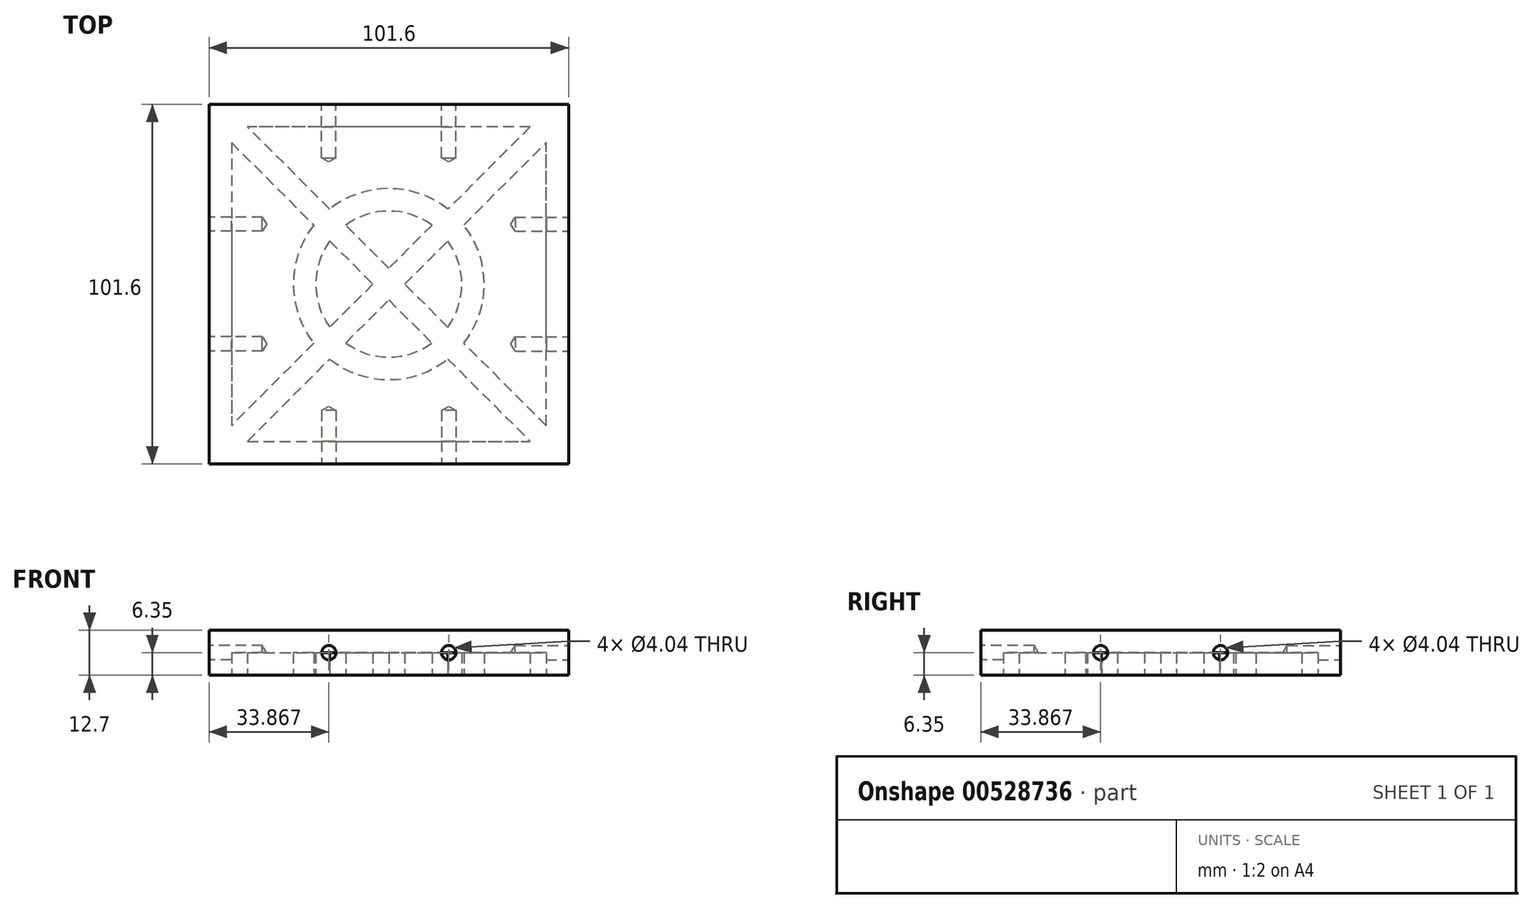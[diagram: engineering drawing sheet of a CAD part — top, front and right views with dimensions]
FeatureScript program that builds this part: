
annotation { "Feature Type Name" : "Feature", "Feature Type Description" : "" }
export const myFeature = defineFeature(function(context is Context, id is Id, definition is map)
    precondition{}
    {
        {
            var Q0;
            Q0=qCreatedBy(makeId("Top.planeOp"),FACE);
            var sketch = newSketch(context, id + "F0", { "sketchPlane" : qUnion([Q0])});
            skLineSegment(sketch, "E0.bottom", {"start": v(50.8, -50.8) * mm, "end": v(-50.8, -50.8) * mm});
            skLineSegment(sketch, "E0.top", {"start": v(50.8, 50.8) * mm, "end": v(-50.8, 50.8) * mm});
            skLineSegment(sketch, "E0.left", {"start": v(50.8, -50.8) * mm, "end": v(50.8, 50.8) * mm});
            skLineSegment(sketch, "E0.right", {"start": v(-50.8, -50.8) * mm, "end": v(-50.8, 50.8) * mm});
            skPoint(sketch, "E0.middle", {"position": v(0, 0) * mm});
            skSolve(sketch);
        }
        {
            var Q0;
            Q0 = qSketchRegion(id + "F0", true);
            extrude(context, id + "F1", {"entities" : qUnion([Q0]), "depth" : 12.7 * mm, "offsetDistance" : 25.4 * mm});
        }
        {
            var Q0;
            Q0=makeQuery(id+"F1.opExtrude","CAP_FACE",FACE,{"disambiguationData":[OSD([sQuery(id+"F0.wireOp",EDGE,"E0.bottom"),sQuery(id+"F0.wireOp",EDGE,"E0.top"),sQuery(id+"F0.wireOp",EDGE,"E0.left"),sQuery(id+"F0.wireOp",EDGE,"E0.right")])],"isStart":true});
            var sketch = newSketch(context, id + "F2", { "sketchPlane" : qUnion([Q0])});
            skLineSegment(sketch, "E1", {"start": v(-50.8, 50.8) * mm, "end": v(0, 0) * mm, "construction": true});
            skLineSegment(sketch, "E2", {"start": v(0, 0) * mm, "end": v(50.8, 50.8) * mm, "construction": true});
            skLineSegment(sketch, "E3.0", {"start": v(0, 4.5) * mm, "end": v(12.17, 16.66) * mm});
            skLineSegment(sketch, "E3.1", {"start": v(-39.96, 44.45) * mm, "end": v(-16.7, 21.2) * mm});
            skLineSegment(sketch, "E4", {"start": v(-39.96, 44.45) * mm, "end": v(39.96, 44.45) * mm});
            skLineSegment(sketch, "E5.1.0", {"start": v(-44.45, -39.96) * mm, "end": v(-44.45, 39.96) * mm});
            skLineSegment(sketch, "E5.1.1", {"start": v(-44.45, -39.96) * mm, "end": v(-21.2, -16.7) * mm});
            skLineSegment(sketch, "E5.1.2", {"start": v(-4.5, 0) * mm, "end": v(-16.66, 12.17) * mm});
            skLineSegment(sketch, "E5.2.0", {"start": v(39.96, -44.45) * mm, "end": v(-39.96, -44.45) * mm});
            skLineSegment(sketch, "E5.2.1", {"start": v(39.96, -44.45) * mm, "end": v(16.7, -21.2) * mm});
            skLineSegment(sketch, "E5.2.2", {"start": v(0, -4.5) * mm, "end": v(-12.17, -16.66) * mm});
            skLineSegment(sketch, "E5.3.0", {"start": v(44.45, 39.96) * mm, "end": v(44.45, -39.96) * mm});
            skLineSegment(sketch, "E5.3.1", {"start": v(44.45, 39.96) * mm, "end": v(21.2, 16.7) * mm});
            skLineSegment(sketch, "E5.3.2", {"start": v(4.5, 0) * mm, "end": v(16.66, -12.17) * mm});
            skPoint(sketch, "E5.center", {"position": v(0, 0) * mm});
            skArc(sketch, "E6", {"start": v(-21.2, 16.7) * mm, "mid": v(-26.99, 0) * mm, "end": v(-21.2, -16.7) * mm});
            skArc(sketch, "E7", {"start": v(-16.66, 12.17) * mm, "mid": v(-20.64, 0) * mm, "end": v(-16.66, -12.17) * mm});
            skLineSegment(sketch, "E8.trimOffspring", {"start": v(-12.17, 16.66) * mm, "end": v(0, 4.5) * mm});
            skLineSegment(sketch, "E9.trimOffspring", {"start": v(-21.2, 16.7) * mm, "end": v(-44.45, 39.96) * mm});
            skArc(sketch, "E10.trimOffspring", {"start": v(-12.17, -16.66) * mm, "mid": v(0, -20.64) * mm, "end": v(12.17, -16.66) * mm});
            skArc(sketch, "E11.trimOffspring", {"start": v(-16.7, -21.2) * mm, "mid": v(0, -26.99) * mm, "end": v(16.7, -21.2) * mm});
            skLineSegment(sketch, "E12.trimOffspring", {"start": v(-16.66, -12.17) * mm, "end": v(-4.5, 0) * mm});
            skLineSegment(sketch, "E13.trimOffspring", {"start": v(-16.7, -21.2) * mm, "end": v(-39.96, -44.45) * mm});
            skLineSegment(sketch, "E14.trimOffspring", {"start": v(12.17, -16.66) * mm, "end": v(0, -4.5) * mm});
            skLineSegment(sketch, "E15.trimOffspring", {"start": v(21.2, -16.7) * mm, "end": v(44.45, -39.96) * mm});
            skArc(sketch, "E16.trimOffspring", {"start": v(16.66, -12.17) * mm, "mid": v(20.64, 0) * mm, "end": v(16.66, 12.17) * mm});
            skArc(sketch, "E17.trimOffspring", {"start": v(21.2, -16.7) * mm, "mid": v(26.99, 0) * mm, "end": v(21.2, 16.7) * mm});
            skArc(sketch, "E18.trimOffspring", {"start": v(16.7, 21.2) * mm, "mid": v(0, 26.99) * mm, "end": v(-16.7, 21.2) * mm});
            skArc(sketch, "E19.trimOffspring", {"start": v(12.17, 16.66) * mm, "mid": v(0, 20.64) * mm, "end": v(-12.17, 16.66) * mm});
            skLineSegment(sketch, "E20.trimOffspring", {"start": v(16.7, 21.2) * mm, "end": v(39.96, 44.45) * mm});
            skLineSegment(sketch, "E21.trimOffspring", {"start": v(16.66, 12.17) * mm, "end": v(4.5, 0) * mm});
            skSolve(sketch);
        }
        {
            var Q0;
            Q0 = qSketchRegion(id + "F2", true);
            extrude(context, id + "F3", {"entities" : qUnion([Q0]), "operationType" : NewBodyOperationType.REMOVE, "oppositeDirection" : true, "depth" : 6.35 * mm, "offsetDistance" : 25.4 * mm});
        }
        {
            var Q0;
            Q0=makeQuery(id+"F1.opExtrude","SWEPT_FACE",FACE,{"disambiguationData":[OSD([sQuery(id+"F0.wireOp",EDGE,"E0.bottom")])]});
            var sketch = newSketch(context, id + "F4", { "sketchPlane" : qUnion([Q0])});
            skLineSegment(sketch, "E22", {"start": v(-50.8, 6.35) * mm, "end": v(50.8, 6.35) * mm, "construction": true});
            skPoint(sketch, "E23", {"position": v(-16.93, 6.35) * mm});
            skPoint(sketch, "E24", {"position": v(16.93, 6.35) * mm});
            skSolve(sketch);
        }
        {
            var Q0;
            Q0=makeQuery(id+"F1.opExtrude","SWEPT_FACE",FACE,{"disambiguationData":[OSD([sQuery(id+"F0.wireOp",EDGE,"E0.left")])]});
            var sketch = newSketch(context, id + "F5", { "sketchPlane" : qUnion([Q0])});
            skLineSegment(sketch, "E25", {"start": v(-50.8, 6.35) * mm, "end": v(50.8, 6.35) * mm, "construction": true});
            skPoint(sketch, "E26", {"position": v(-16.93, 6.35) * mm});
            skPoint(sketch, "E27", {"position": v(16.93, 6.35) * mm});
            skSolve(sketch);
        }
        {
            var Q0;
            Q0=makeQuery(id+"F1.opExtrude","SWEPT_FACE",FACE,{"disambiguationData":[OSD([sQuery(id+"F0.wireOp",EDGE,"E0.top")])]});
            var sketch = newSketch(context, id + "F6", { "sketchPlane" : qUnion([Q0])});
            skLineSegment(sketch, "E28", {"start": v(-50.8, 6.35) * mm, "end": v(50.8, 6.35) * mm, "construction": true});
            skPoint(sketch, "E29", {"position": v(-16.93, 6.35) * mm});
            skPoint(sketch, "E30", {"position": v(16.93, 6.35) * mm});
            skSolve(sketch);
        }
        {
            var Q0;
            Q0=makeQuery(id+"F1.opExtrude","SWEPT_FACE",FACE,{"disambiguationData":[OSD([sQuery(id+"F0.wireOp",EDGE,"E0.right")])]});
            var sketch = newSketch(context, id + "F7", { "sketchPlane" : qUnion([Q0])});
            skLineSegment(sketch, "E31", {"start": v(-50.8, 6.35) * mm, "end": v(50.8, 6.35) * mm, "construction": true});
            skPoint(sketch, "E32", {"position": v(-16.93, 6.35) * mm});
            skPoint(sketch, "E33", {"position": v(16.93, 6.35) * mm});
            skSolve(sketch);
        }
        {
            var Q0;
            Q0=sQuery(id+"F4.wireOp",VERTEX,"E23");
            var Q1;
            Q1=sQuery(id+"F4.wireOp",VERTEX,"E24");
            var Q2;
            Q2=sQuery(id+"F7.wireOp",VERTEX,"E33");
            var Q3;
            Q3=sQuery(id+"F7.wireOp",VERTEX,"E32");
            var Q4;
            Q4=sQuery(id+"F6.wireOp",VERTEX,"E30");
            var Q5;
            Q5=sQuery(id+"F6.wireOp",VERTEX,"E29");
            var Q6;
            Q6=sQuery(id+"F5.wireOp",VERTEX,"E27");
            var Q7;
            Q7=sQuery(id+"F5.wireOp",VERTEX,"E26");
            var Q8;
            Q8=makeQuery(id+"F1.opExtrude","SWEPT_BODY",BODY,{"disambiguationData":[OSD([sQuery(id+"F0.wireOp",EDGE,"E0.bottom"),sQuery(id+"F0.wireOp",EDGE,"E0.top"),sQuery(id+"F0.wireOp",EDGE,"E0.left"),sQuery(id+"F0.wireOp",EDGE,"E0.right")])]});
            hole(context, id + "F8", {"style" : HoleStyle.SIMPLE, "endStyle" : HoleEndStyle.BLIND, "standardTappedOrClearance" : lookupTablePath({ "standard" : "ANSI", "engagement" : "75%", "pitch" : "32 tpi", "size" : "#10", "type" : "Tapped" }), "standardBlindInLast" : lookupTablePath({ "standard" : "ANSI", "engagement" : "75%", "pitch" : "32 tpi", "size" : "#10", "type" : "Tapped" }), "holeDiameter" : 4.04 * mm, "showTappedDepth" : true, "holeDepth" : 15.08 * mm, "isTappedThrough" : true, "tappedDepth" : 12.7 * mm, "tapClearance" : 3, "locations" : qUnion([Q0, Q1, Q2, Q3, Q4, Q5, Q6, Q7]), "scope" : qUnion([Q8]), "majorDiameter" : 4.83 * mm});
        }
    });
